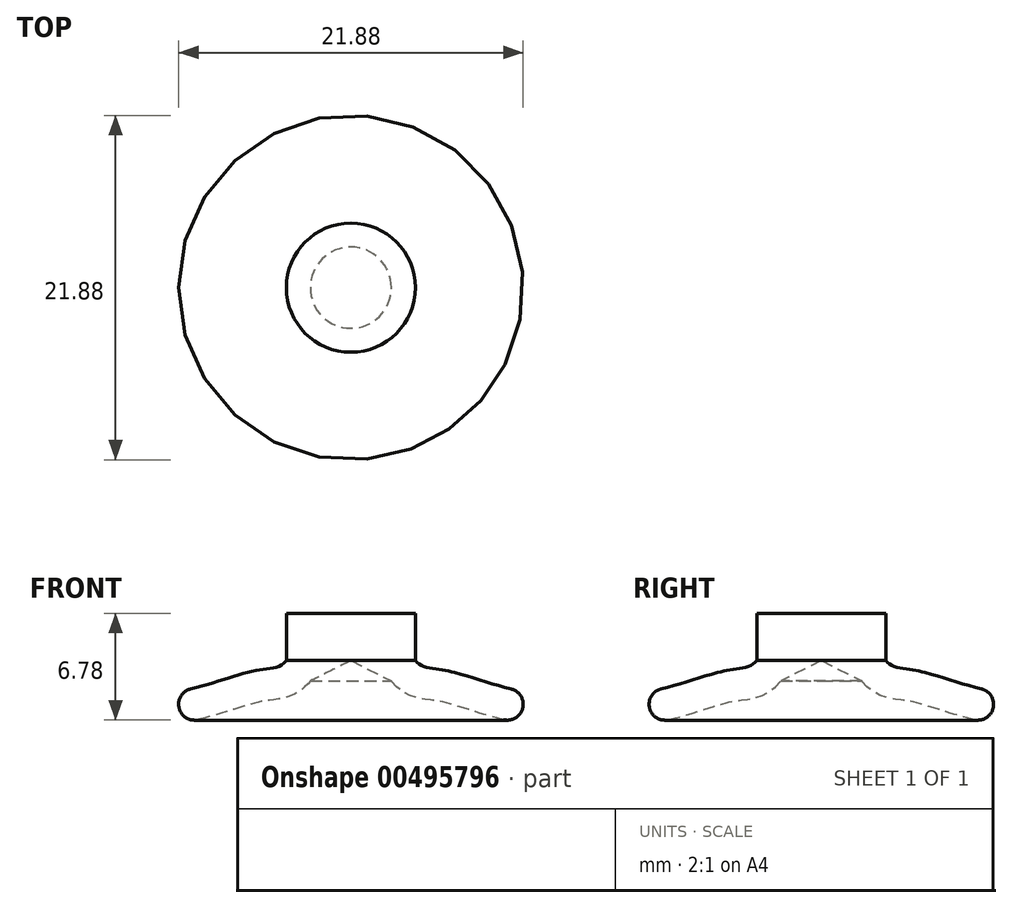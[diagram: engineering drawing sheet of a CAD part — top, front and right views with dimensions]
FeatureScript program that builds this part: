
annotation { "Feature Type Name" : "Feature", "Feature Type Description" : "" }
export const myFeature = defineFeature(function(context is Context, id is Id, definition is map)
    precondition{}
    {
        {
            var Q0;
            Q0=qCreatedBy(makeId("Front.planeOp"),FACE);
            var sketch = newSketch(context, id + "F0", { "sketchPlane" : qUnion([Q0])});
            skLineSegment(sketch, "E0.bottom", {"start": v(-3.1, 2) * mm, "end": v(1, 2) * mm});
            skLineSegment(sketch, "E0.top", {"start": v(-3.1, 5) * mm, "end": v(1, 5) * mm});
            skLineSegment(sketch, "E0.left", {"start": v(-3.1, 2) * mm, "end": v(-3.1, 5) * mm});
            skLineSegment(sketch, "E0.right", {"start": v(1, 2) * mm, "end": v(1, 5) * mm});
            skFitSpline(sketch, "E1", {"points": [v(-3.1, 2) * mm, v(-4.9, 1.4) * mm, v(-10.1, 0) * mm], "startDerivative": vector(-3.68, -4.33) * mm, "endDerivative": vector(-9.91, -1.83) * mm});
            skFitSpline(sketch, "E2.0", {"points": [v(-1.57, 0.7) * mm, v(-1.74, 0.5) * mm, v(-2.15, 0.12) * mm, v(-2.85, -0.25) * mm, v(-3.47, -0.42) * mm, v(-3.95, -0.5) * mm, v(-4.24, -0.53) * mm, v(-4.44, -0.56) * mm, v(-4.57, -0.58) * mm, v(-4.7, -0.6) * mm, v(-4.9, -0.65) * mm, v(-5.2, -0.73) * mm, v(-5.63, -0.85) * mm, v(-6.25, -1.04) * mm, v(-7.15, -1.32) * mm, v(-8.36, -1.67) * mm, v(-9.26, -1.88) * mm, v(-9.73, -1.97) * mm]});
            skLineSegment(sketch, "E3", {"start": v(-10.1, 0) * mm, "end": v(-9.73, -1.97) * mm});
            skLineSegment(sketch, "E4", {"start": v(-1.57, 0.7) * mm, "end": v(1, 2) * mm});
            skSolve(sketch);
        }
        {
            var Q0;
            {var subQ0=sQuery(id+"F0.wireOp",EDGE,"E1");Q0=makeQuery(id+"F0.imprint","IMPRINT",FACE,{"disambiguationData":[TD([[makeQuery(id+"F0.imprint","IMPRINT",EDGE,{"derivedFrom":subQ0}),1.0]])]});}
            var Q1;
            Q1=makeQuery(id+"F0.imprint","IMPRINT",FACE,{"disambiguationData":[TD([[makeQuery(id+"F0.imprint","IMPRINT",EDGE,{"derivedFrom":sQuery(id+"F0.wireOp",EDGE,"E0.top")}),-1.0]])]});
            var Q2;
            Q2=sQuery(id+"F0.wireOp",EDGE,"E0.right");
            revolve(context, id + "F1", {"entities" : qUnion([Q0, Q1]), "axis" : qUnion([Q2]), "revolveType" : RevolveType.FULL});
        }
        {
            var Q0;
            Q0=makeQuery(id+"F1.opRevolve","SWEPT_EDGE",EDGE,{"disambiguationData":[OSD([sQuery(id+"F0.wireOp",EDGE,"E2.0"),sQuery(id+"F0.wireOp",EDGE,"E3")])]});
            var Q1;
            Q1=makeQuery(id+"F1.opRevolve","SWEPT_EDGE",EDGE,{"disambiguationData":[OSD([sQuery(id+"F0.wireOp",EDGE,"E1"),sQuery(id+"F0.wireOp",EDGE,"E3")])]});
            fillet(context, id + "F2", {"entities" : qUnion([Q0, Q1]), "radius" : 1 * mm, "tangentPropagation" : true, "allowEdgeOverflow" : false});
        }
    });
